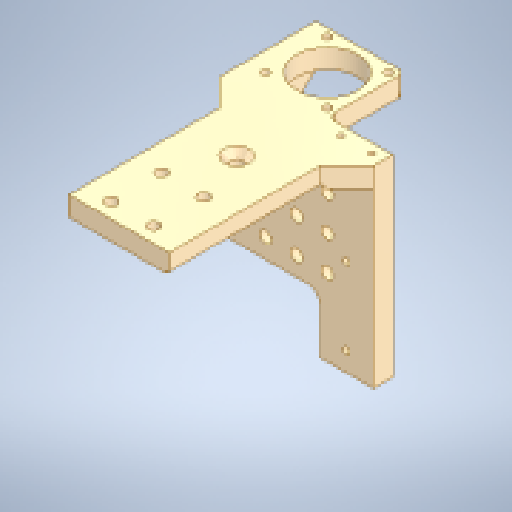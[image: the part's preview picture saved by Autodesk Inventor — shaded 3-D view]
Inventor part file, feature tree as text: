
AUTODESK INVENTOR PART (.ipt)
format: ipt  version: 2024.1 (Build 281209000, 209)  size: 360,960 bytes
history: native  units: in
note: dims shown in document units (in); Inventor stores cm internally (conversion verified against a paired STEP export)
features: extrude x12, sketch x12, fillet x6, chamfer x4
ambient origin geometry x8: Origin, YZ Plane, XZ Plane, XY Plane, X Axis, Y Axis, Z Axis, Center Point
bodies: Solid1 (feature_tree)
feature tree (34):
  extrude  "Extrusion1"  Depth=1.378in
  extrude  "Extrusion2"  Depth=0.1969in
  extrude  "Extrusion3"  Depth=0.1969in TaperAngle=0.0deg
  extrude  "Extrusion4"  Depth=0.1181in
  fillet  "Fillet1"  Radius=0.7874in
  extrude  "Extrusion5"  Depth=0.3937in
  fillet  "Fillet2"  Radius=0.3937in
  fillet  "Fillet4"  Radius=0.0787in
  extrude  "Extrusion6"  Depth=0.0787in
  chamfer  "Chamfer2"  Distance=0.315in
  extrude  "Extrusion7"  Depth=0.315in
  chamfer  "Chamfer3"  Distance=0.315in
  extrude  "Extrusion8"  TaperAngle=0.0deg  [1 undecoded]
  chamfer  "Chamfer4"  Distance=0.0591in
  fillet  "Fillet5"  [1 undecoded]
  extrude  "Extrusion9"  Depth=0.1969in
  extrude  "Extrusion10"  Depth=0.0787in
  fillet  "Fillet6"  Radius=0.1969in
  extrude  "Extrusion11"  Depth=0.1181in
  chamfer  "Chamfer7"  Distance=0.2756in
  extrude  "Extrusion12"  Depth=0.1181in TaperAngle=0.0deg
  fillet  "Fillet7"  Radius=0.0787in
  sketch  "Sketch1"  dims[d0=1.5748in d1=1.378in]
  sketch  "Sketch2"  dims[d2=0.1969in d3=0.0in d4=0.9055in]
  sketch  "Sketch3"  dims[d5=0.1969in d6=0.7874in d7=0.0in]
  sketch  "Sketch4"  dims[d8=0.7874in d9=0.1181in d10=0.7874in d11=0.0in]
  sketch  "Sketch5"  dims[d12=0.6299in d13=0.3937in d14=0.3937in d15=0.0787in]
  sketch  "Sketch6"  dims[d16=0.0787in d17=0.0787in]
  sketch  "Sketch7"  dims[d18=0.0787in]
  sketch  "Sketch8"  dims[d19=0.315in]
  sketch  "Sketch9"  dims[d20=0.315in]
  sketch  "Sketch10"  dims[d21=0.315in]
  sketch  "Sketch11"  dims[d22=0.315in]
  sketch  "Sketch12"  dims[d23=0.315in d24=0.315in d25=0.315in d26=0.315in d27=0.0in d28=0.0in d29=0.0591in d30=0.0in d31=0.0in d32=0.1969in d34=0.0787in d39=0.1969in d40=0.2756in d41=0.2756in d42=1.811in d43=0.0in d44=0.2756in d45=0.0787in d46=45.0deg d47=0.1181in d48=0.6102in d49=0.5118in d50=0.0in d51=0.0in d52=0.0709in d53=0.0787in d54=45.0deg d55=0.063in d56=0.063in d57=0.0984in d58=0.0984in d59=0.1181in d60=0.315in d61=0.3937in d62=0.0in d63=0.0315in d64=0.0787in d65=45.0deg d66=0.0394in d67=0.5512in d68=0.5906in d69=0.0in d70=0.063in d71=0.2756in d72=0.1969in d73=1.1811in d75=0.7874in d76=0.3937in d78=0.3937in d80=0.0in d81=0.0in d88=0.1181in d89=0.1181in d90=0.1181in d91=0.1181in d92=0.1181in d93=0.1181in d94=0.1181in d95=0.1969in d96=0.1969in d97=0.315in d98=0.4724in d99=0.4724in d100=0.4724in d101=0.3543in d102=0.3543in d103=0.3543in d104=0.315in d105=0.3543in d106=0.315in d107=0.0in d108=0.0in d109=0.315in d110=0.1181in d111=0.1969in d112=0.3543in d113=0.3543in d114=0.1181in d115=0.1181in d116=0.315in d117=0.315in d118=0.0748in d119=0.0787in d120=45.0deg d121=0.1181in d122=0.1181in d123=0.1181in d124=0.1181in d125=0.6693in d126=0.6693in d127=0.315in d128=0.315in d129=0.2756in d130=0.2756in d131=0.1575in d132=0.1575in d133=0.0in d134=0.0in d138=0.1181in]
note: 2 required parameter values undecoded (feature->parameter linkage not recoverable at this tier; creation-order binding heuristic only, values carry confidence <= 0.55)
